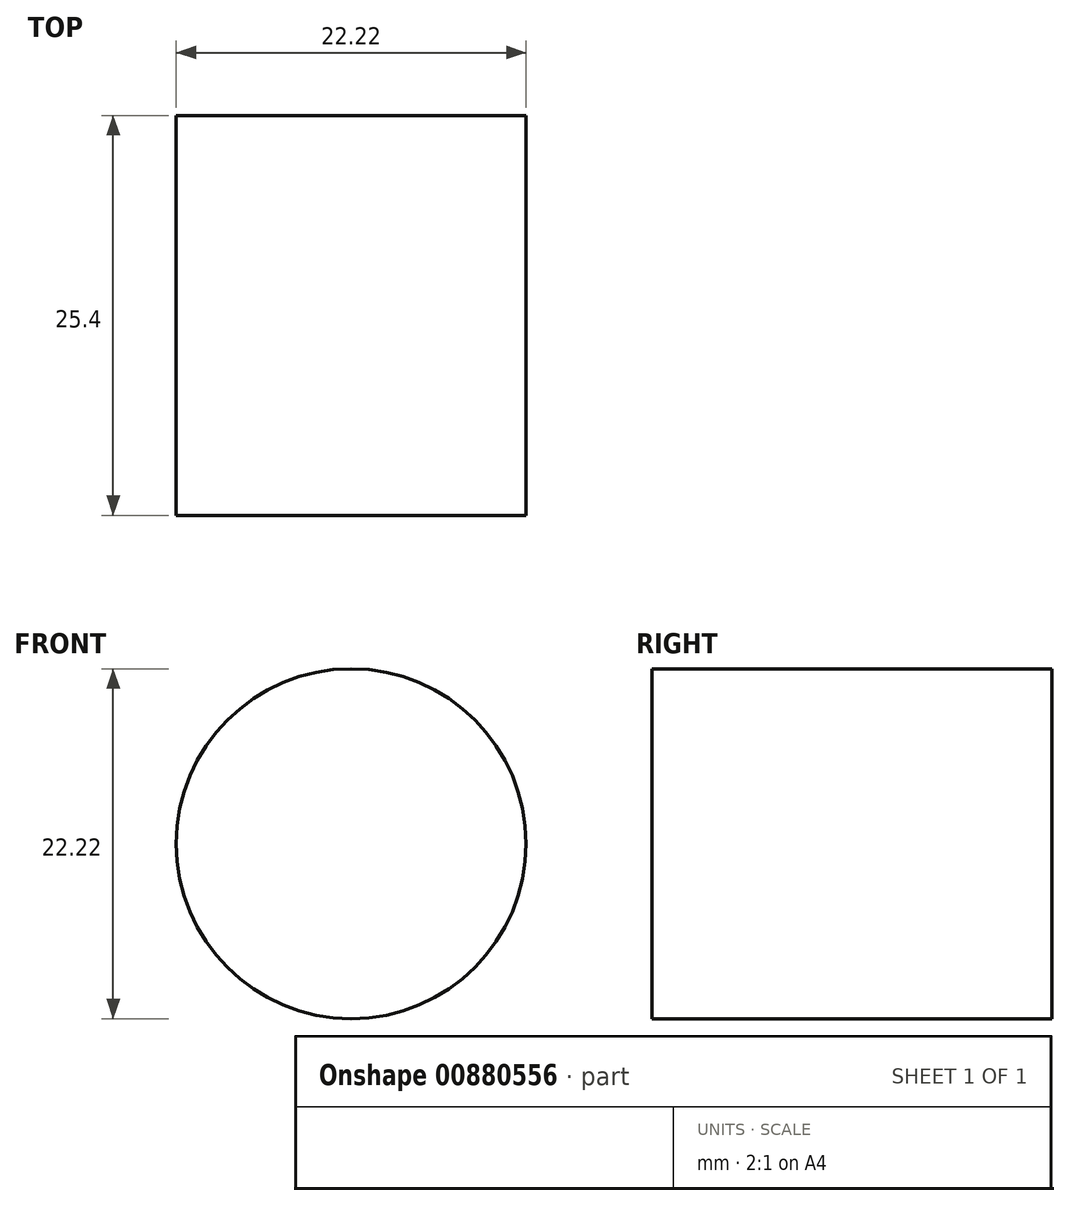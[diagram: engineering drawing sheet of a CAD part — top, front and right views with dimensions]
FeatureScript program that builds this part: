
annotation { "Feature Type Name" : "Feature", "Feature Type Description" : "" }
export const myFeature = defineFeature(function(context is Context, id is Id, definition is map)
    precondition{}
    {
        {
            var Q0;
            Q0=qCreatedBy(makeId("Front.planeOp"),FACE);
            var sketch = newSketch(context, id + "F0", { "sketchPlane" : qUnion([Q0])});
            skCircle(sketch, "E0", {"center": v(0, 0) * mm, "radius": 11.11 * mm});
            skSolve(sketch);
        }
        {
            var Q0;
            Q0 = qSketchRegion(id + "F0", true);
            extrude(context, id + "F1", {"entities" : qUnion([Q0]), "depth" : 25.4 * mm, "offsetDistance" : 25.4 * mm});
        }
    });
